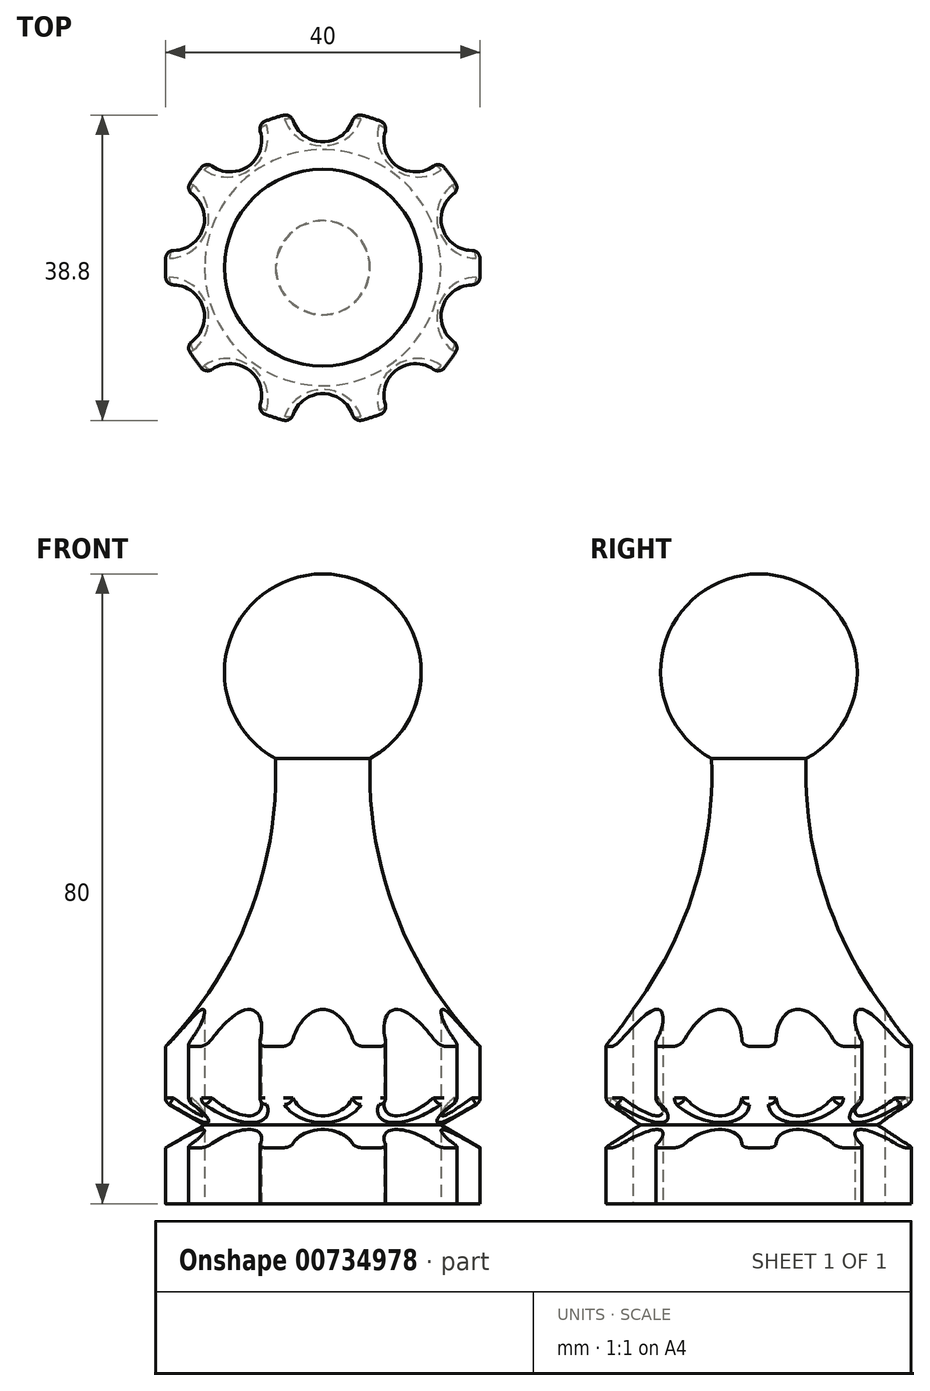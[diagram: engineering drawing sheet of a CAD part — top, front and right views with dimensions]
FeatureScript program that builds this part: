
annotation { "Feature Type Name" : "Feature", "Feature Type Description" : "" }
export const myFeature = defineFeature(function(context is Context, id is Id, definition is map)
    precondition{}
    {
        {
            var Q0;
            Q0=qCreatedBy(makeId("Front.planeOp"),FACE);
            var sketch = newSketch(context, id + "F0", { "sketchPlane" : qUnion([Q0])});
            skLineSegment(sketch, "E0", {"start": v(0, 80) * mm, "end": v(0, 0) * mm});
            skLineSegment(sketch, "E1", {"start": v(0, 0) * mm, "end": v(20, 0) * mm});
            skLineSegment(sketch, "E2", {"start": v(20, 0) * mm, "end": v(20, 7.11) * mm});
            skLineSegment(sketch, "E3", {"start": v(20, 7.11) * mm, "end": v(15, 10) * mm});
            skLineSegment(sketch, "E4", {"start": v(15, 10) * mm, "end": v(20, 12.89) * mm});
            skLineSegment(sketch, "E5", {"start": v(20, 12.89) * mm, "end": v(20, 20) * mm});
            skArc(sketch, "E6", {"start": v(6, 56.53) * mm, "mid": v(9.28, 36.84) * mm, "end": v(20, 20) * mm});
            skArc(sketch, "E7", {"start": v(6, 56.53) * mm, "mid": v(12.11, 70.6) * mm, "end": v(0, 80) * mm});
            skSolve(sketch);
        }
        {
            var Q0;
            Q0=qCreatedBy(makeId("Front.planeOp"),FACE);
            var sketch = newSketch(context, id + "F1", { "sketchPlane" : qUnion([Q0])});
            skLineSegment(sketch, "E8", {"start": v(0, -54.33) * mm, "end": v(0, 51.9) * mm, "construction": true});
            skSolve(sketch);
        }
        {
            var Q0;
            Q0 = qSketchRegion(id + "F0", true);
            var Q1;
            Q1=sQuery(id+"F1.wireOp",EDGE,"E8");
            revolve(context, id + "F2", {"surfaceOperationType" : NewSurfaceOperationType.NEW, "entities" : qUnion([Q0]), "axis" : qUnion([Q1]), "revolveType" : RevolveType.FULL});
        }
        {
            var Q0;
            Q0=makeQuery(id+"F2.opRevolve","SWEPT_FACE",FACE,{"disambiguationData":[OSD([sQuery(id+"F0.wireOp",EDGE,"E1")])]});
            var sketch = newSketch(context, id + "F3", { "sketchPlane" : qUnion([Q0])});
            skCircle(sketch, "E9", {"center": v(0, 20) * mm, "radius": 4 * mm});
            skCircle(sketch, "E10.1.0", {"center": v(-11.76, 16.18) * mm, "radius": 4 * mm});
            skCircle(sketch, "E10.2.0", {"center": v(-19.02, 6.18) * mm, "radius": 4 * mm});
            skCircle(sketch, "E10.3.0", {"center": v(-19.02, -6.18) * mm, "radius": 4 * mm});
            skCircle(sketch, "E10.4.0", {"center": v(-11.76, -16.18) * mm, "radius": 4 * mm});
            skCircle(sketch, "E10.5.0", {"center": v(0, -20) * mm, "radius": 4 * mm});
            skCircle(sketch, "E10.6.0", {"center": v(11.76, -16.18) * mm, "radius": 4 * mm});
            skCircle(sketch, "E10.7.0", {"center": v(19.02, -6.18) * mm, "radius": 4 * mm});
            skCircle(sketch, "E10.8.0", {"center": v(19.02, 6.18) * mm, "radius": 4 * mm});
            skCircle(sketch, "E10.9.0", {"center": v(11.76, 16.18) * mm, "radius": 4 * mm});
            skPoint(sketch, "E10.center", {"position": v(0, 0) * mm});
            skSolve(sketch);
        }
        {
            var Q0;
            {var subQ0=sQuery(id+"F3.wireOp",EDGE,"E9");var subQ1=makeQuery(id+"F2.opRevolve","SWEPT_EDGE",EDGE,{"disambiguationData":[OSD([sQuery(id+"F0.wireOp",EDGE,"E1"),sQuery(id+"F0.wireOp",EDGE,"E2")])]});var subQ2=makeQuery(id+"F3.imprint","INTERSECT",VERTEX,{"disambiguationData":[OD(0.0)],"derivedFrom":[subQ1,subQ0]});Q0=makeQuery(id+"F3.imprint","IMPRINT",FACE,{"disambiguationData":[TD([[makeQuery(id+"F3.imprint","IMPRINT",EDGE,{"disambiguationData":[TD([[subQ2,1.0]])],"derivedFrom":subQ0}),1.0]])]});}
            var Q1;
            {var subQ0=sQuery(id+"F3.wireOp",EDGE,"E9");var subQ1=makeQuery(id+"F2.opRevolve","SWEPT_EDGE",EDGE,{"disambiguationData":[OSD([sQuery(id+"F0.wireOp",EDGE,"E1"),sQuery(id+"F0.wireOp",EDGE,"E2")])]});var subQ2=makeQuery(id+"F3.imprint","INTERSECT",VERTEX,{"disambiguationData":[OD(0.0)],"derivedFrom":[subQ1,subQ0]});Q1=makeQuery(id+"F3.imprint","IMPRINT",FACE,{"disambiguationData":[TD([[makeQuery(id+"F3.imprint","IMPRINT",EDGE,{"disambiguationData":[TD([[subQ2,-1.0]])],"derivedFrom":subQ0}),1.0]])]});}
            var Q2;
            {var subQ0=sQuery(id+"F3.wireOp",EDGE,"E10.1.0");var subQ1=makeQuery(id+"F2.opRevolve","SWEPT_EDGE",EDGE,{"disambiguationData":[OSD([sQuery(id+"F0.wireOp",EDGE,"E1"),sQuery(id+"F0.wireOp",EDGE,"E2")])]});var subQ2=makeQuery(id+"F3.imprint","INTERSECT",VERTEX,{"disambiguationData":[OD(0.0)],"derivedFrom":[subQ1,subQ0]});Q2=makeQuery(id+"F3.imprint","IMPRINT",FACE,{"disambiguationData":[TD([[makeQuery(id+"F3.imprint","IMPRINT",EDGE,{"disambiguationData":[TD([[subQ2,-1.0]])],"derivedFrom":subQ0}),1.0]])]});}
            var Q3;
            {var subQ0=sQuery(id+"F3.wireOp",EDGE,"E10.1.0");var subQ1=makeQuery(id+"F2.opRevolve","SWEPT_EDGE",EDGE,{"disambiguationData":[OSD([sQuery(id+"F0.wireOp",EDGE,"E1"),sQuery(id+"F0.wireOp",EDGE,"E2")])]});var subQ2=makeQuery(id+"F3.imprint","INTERSECT",VERTEX,{"disambiguationData":[OD(0.0)],"derivedFrom":[subQ1,subQ0]});Q3=makeQuery(id+"F3.imprint","IMPRINT",FACE,{"disambiguationData":[TD([[makeQuery(id+"F3.imprint","IMPRINT",EDGE,{"disambiguationData":[TD([[subQ2,1.0]])],"derivedFrom":subQ0}),1.0]])]});}
            var Q4;
            {var subQ0=sQuery(id+"F3.wireOp",EDGE,"E10.2.0");var subQ1=makeQuery(id+"F2.opRevolve","SWEPT_EDGE",EDGE,{"disambiguationData":[OSD([sQuery(id+"F0.wireOp",EDGE,"E1"),sQuery(id+"F0.wireOp",EDGE,"E2")])]});var subQ2=makeQuery(id+"F3.imprint","INTERSECT",VERTEX,{"disambiguationData":[OD(0.0)],"derivedFrom":[subQ1,subQ0]});Q4=makeQuery(id+"F3.imprint","IMPRINT",FACE,{"disambiguationData":[TD([[makeQuery(id+"F3.imprint","IMPRINT",EDGE,{"disambiguationData":[TD([[subQ2,1.0]])],"derivedFrom":subQ0}),1.0]])]});}
            var Q5;
            {var subQ0=sQuery(id+"F3.wireOp",EDGE,"E10.2.0");var subQ1=makeQuery(id+"F2.opRevolve","SWEPT_EDGE",EDGE,{"disambiguationData":[OSD([sQuery(id+"F0.wireOp",EDGE,"E1"),sQuery(id+"F0.wireOp",EDGE,"E2")])]});var subQ2=makeQuery(id+"F3.imprint","INTERSECT",VERTEX,{"disambiguationData":[OD(0.0)],"derivedFrom":[subQ1,subQ0]});Q5=makeQuery(id+"F3.imprint","IMPRINT",FACE,{"disambiguationData":[TD([[makeQuery(id+"F3.imprint","IMPRINT",EDGE,{"disambiguationData":[TD([[subQ2,-1.0]])],"derivedFrom":subQ0}),1.0]])]});}
            var Q6;
            {var subQ0=sQuery(id+"F3.wireOp",EDGE,"E10.3.0");var subQ1=makeQuery(id+"F2.opRevolve","SWEPT_EDGE",EDGE,{"disambiguationData":[OSD([sQuery(id+"F0.wireOp",EDGE,"E1"),sQuery(id+"F0.wireOp",EDGE,"E2")])]});var subQ2=makeQuery(id+"F3.imprint","INTERSECT",VERTEX,{"disambiguationData":[OD(0.0)],"derivedFrom":[subQ1,subQ0]});Q6=makeQuery(id+"F3.imprint","IMPRINT",FACE,{"disambiguationData":[TD([[makeQuery(id+"F3.imprint","IMPRINT",EDGE,{"disambiguationData":[TD([[subQ2,1.0]])],"derivedFrom":subQ0}),1.0]])]});}
            var Q7;
            {var subQ0=sQuery(id+"F3.wireOp",EDGE,"E10.3.0");var subQ1=makeQuery(id+"F2.opRevolve","SWEPT_EDGE",EDGE,{"disambiguationData":[OSD([sQuery(id+"F0.wireOp",EDGE,"E1"),sQuery(id+"F0.wireOp",EDGE,"E2")])]});var subQ2=makeQuery(id+"F3.imprint","INTERSECT",VERTEX,{"disambiguationData":[OD(0.0)],"derivedFrom":[subQ1,subQ0]});Q7=makeQuery(id+"F3.imprint","IMPRINT",FACE,{"disambiguationData":[TD([[makeQuery(id+"F3.imprint","IMPRINT",EDGE,{"disambiguationData":[TD([[subQ2,-1.0]])],"derivedFrom":subQ0}),1.0]])]});}
            var Q8;
            {var subQ0=sQuery(id+"F3.wireOp",EDGE,"E10.4.0");var subQ1=makeQuery(id+"F2.opRevolve","SWEPT_EDGE",EDGE,{"disambiguationData":[OSD([sQuery(id+"F0.wireOp",EDGE,"E1"),sQuery(id+"F0.wireOp",EDGE,"E2")])]});var subQ2=makeQuery(id+"F3.imprint","INTERSECT",VERTEX,{"disambiguationData":[OD(0.0)],"derivedFrom":[subQ1,subQ0]});Q8=makeQuery(id+"F3.imprint","IMPRINT",FACE,{"disambiguationData":[TD([[makeQuery(id+"F3.imprint","IMPRINT",EDGE,{"disambiguationData":[TD([[subQ2,-1.0]])],"derivedFrom":subQ0}),1.0]])]});}
            var Q9;
            {var subQ0=sQuery(id+"F3.wireOp",EDGE,"E10.4.0");var subQ1=makeQuery(id+"F2.opRevolve","SWEPT_EDGE",EDGE,{"disambiguationData":[OSD([sQuery(id+"F0.wireOp",EDGE,"E1"),sQuery(id+"F0.wireOp",EDGE,"E2")])]});var subQ2=makeQuery(id+"F3.imprint","INTERSECT",VERTEX,{"disambiguationData":[OD(0.0)],"derivedFrom":[subQ1,subQ0]});Q9=makeQuery(id+"F3.imprint","IMPRINT",FACE,{"disambiguationData":[TD([[makeQuery(id+"F3.imprint","IMPRINT",EDGE,{"disambiguationData":[TD([[subQ2,1.0]])],"derivedFrom":subQ0}),1.0]])]});}
            var Q10;
            {var subQ0=sQuery(id+"F3.wireOp",EDGE,"E10.5.0");var subQ1=makeQuery(id+"F2.opRevolve","SWEPT_EDGE",EDGE,{"disambiguationData":[OSD([sQuery(id+"F0.wireOp",EDGE,"E1"),sQuery(id+"F0.wireOp",EDGE,"E2")])]});var subQ2=makeQuery(id+"F3.imprint","INTERSECT",VERTEX,{"disambiguationData":[OD(0.0)],"derivedFrom":[subQ1,subQ0]});Q10=makeQuery(id+"F3.imprint","IMPRINT",FACE,{"disambiguationData":[TD([[makeQuery(id+"F3.imprint","IMPRINT",EDGE,{"disambiguationData":[TD([[subQ2,-1.0]])],"derivedFrom":subQ0}),1.0]])]});}
            var Q11;
            {var subQ0=sQuery(id+"F3.wireOp",EDGE,"E10.5.0");var subQ1=makeQuery(id+"F2.opRevolve","SWEPT_EDGE",EDGE,{"disambiguationData":[OSD([sQuery(id+"F0.wireOp",EDGE,"E1"),sQuery(id+"F0.wireOp",EDGE,"E2")])]});var subQ2=makeQuery(id+"F3.imprint","INTERSECT",VERTEX,{"disambiguationData":[OD(0.0)],"derivedFrom":[subQ1,subQ0]});Q11=makeQuery(id+"F3.imprint","IMPRINT",FACE,{"disambiguationData":[TD([[makeQuery(id+"F3.imprint","IMPRINT",EDGE,{"disambiguationData":[TD([[subQ2,1.0]])],"derivedFrom":subQ0}),1.0]])]});}
            var Q12;
            {var subQ0=sQuery(id+"F3.wireOp",EDGE,"E10.6.0");var subQ1=makeQuery(id+"F2.opRevolve","SWEPT_EDGE",EDGE,{"disambiguationData":[OSD([sQuery(id+"F0.wireOp",EDGE,"E1"),sQuery(id+"F0.wireOp",EDGE,"E2")])]});var subQ2=makeQuery(id+"F3.imprint","INTERSECT",VERTEX,{"disambiguationData":[OD(0.0)],"derivedFrom":[subQ1,subQ0]});Q12=makeQuery(id+"F3.imprint","IMPRINT",FACE,{"disambiguationData":[TD([[makeQuery(id+"F3.imprint","IMPRINT",EDGE,{"disambiguationData":[TD([[subQ2,-1.0]])],"derivedFrom":subQ0}),1.0]])]});}
            var Q13;
            {var subQ0=sQuery(id+"F3.wireOp",EDGE,"E10.6.0");var subQ1=makeQuery(id+"F2.opRevolve","SWEPT_EDGE",EDGE,{"disambiguationData":[OSD([sQuery(id+"F0.wireOp",EDGE,"E1"),sQuery(id+"F0.wireOp",EDGE,"E2")])]});var subQ2=makeQuery(id+"F3.imprint","INTERSECT",VERTEX,{"disambiguationData":[OD(0.0)],"derivedFrom":[subQ1,subQ0]});Q13=makeQuery(id+"F3.imprint","IMPRINT",FACE,{"disambiguationData":[TD([[makeQuery(id+"F3.imprint","IMPRINT",EDGE,{"disambiguationData":[TD([[subQ2,1.0]])],"derivedFrom":subQ0}),1.0]])]});}
            var Q14;
            {var subQ0=sQuery(id+"F3.wireOp",EDGE,"E10.7.0");var subQ1=makeQuery(id+"F2.opRevolve","SWEPT_EDGE",EDGE,{"disambiguationData":[OSD([sQuery(id+"F0.wireOp",EDGE,"E1"),sQuery(id+"F0.wireOp",EDGE,"E2")])]});var subQ2=makeQuery(id+"F3.imprint","INTERSECT",VERTEX,{"disambiguationData":[OD(0.0)],"derivedFrom":[subQ1,subQ0]});Q14=makeQuery(id+"F3.imprint","IMPRINT",FACE,{"disambiguationData":[TD([[makeQuery(id+"F3.imprint","IMPRINT",EDGE,{"disambiguationData":[TD([[subQ2,1.0]])],"derivedFrom":subQ0}),1.0]])]});}
            var Q15;
            {var subQ0=sQuery(id+"F3.wireOp",EDGE,"E10.7.0");var subQ1=makeQuery(id+"F2.opRevolve","SWEPT_EDGE",EDGE,{"disambiguationData":[OSD([sQuery(id+"F0.wireOp",EDGE,"E1"),sQuery(id+"F0.wireOp",EDGE,"E2")])]});var subQ2=makeQuery(id+"F3.imprint","INTERSECT",VERTEX,{"disambiguationData":[OD(0.0)],"derivedFrom":[subQ1,subQ0]});Q15=makeQuery(id+"F3.imprint","IMPRINT",FACE,{"disambiguationData":[TD([[makeQuery(id+"F3.imprint","IMPRINT",EDGE,{"disambiguationData":[TD([[subQ2,-1.0]])],"derivedFrom":subQ0}),1.0]])]});}
            var Q16;
            {var subQ0=sQuery(id+"F3.wireOp",EDGE,"E10.8.0");var subQ1=makeQuery(id+"F2.opRevolve","SWEPT_EDGE",EDGE,{"disambiguationData":[OSD([sQuery(id+"F0.wireOp",EDGE,"E1"),sQuery(id+"F0.wireOp",EDGE,"E2")])]});var subQ2=makeQuery(id+"F3.imprint","INTERSECT",VERTEX,{"disambiguationData":[OD(0.0)],"derivedFrom":[subQ1,subQ0]});Q16=makeQuery(id+"F3.imprint","IMPRINT",FACE,{"disambiguationData":[TD([[makeQuery(id+"F3.imprint","IMPRINT",EDGE,{"disambiguationData":[TD([[subQ2,1.0]])],"derivedFrom":subQ0}),1.0]])]});}
            var Q17;
            {var subQ0=sQuery(id+"F3.wireOp",EDGE,"E10.8.0");var subQ1=makeQuery(id+"F2.opRevolve","SWEPT_EDGE",EDGE,{"disambiguationData":[OSD([sQuery(id+"F0.wireOp",EDGE,"E1"),sQuery(id+"F0.wireOp",EDGE,"E2")])]});var subQ2=makeQuery(id+"F3.imprint","INTERSECT",VERTEX,{"disambiguationData":[OD(0.0)],"derivedFrom":[subQ1,subQ0]});Q17=makeQuery(id+"F3.imprint","IMPRINT",FACE,{"disambiguationData":[TD([[makeQuery(id+"F3.imprint","IMPRINT",EDGE,{"disambiguationData":[TD([[subQ2,-1.0]])],"derivedFrom":subQ0}),1.0]])]});}
            var Q18;
            {var subQ0=sQuery(id+"F3.wireOp",EDGE,"E10.9.0");var subQ1=makeQuery(id+"F2.opRevolve","SWEPT_EDGE",EDGE,{"disambiguationData":[OSD([sQuery(id+"F0.wireOp",EDGE,"E1"),sQuery(id+"F0.wireOp",EDGE,"E2")])]});var subQ2=makeQuery(id+"F3.imprint","INTERSECT",VERTEX,{"disambiguationData":[OD(0.0)],"derivedFrom":[subQ1,subQ0]});Q18=makeQuery(id+"F3.imprint","IMPRINT",FACE,{"disambiguationData":[TD([[makeQuery(id+"F3.imprint","IMPRINT",EDGE,{"disambiguationData":[TD([[subQ2,-1.0]])],"derivedFrom":subQ0}),1.0]])]});}
            var Q19;
            {var subQ0=sQuery(id+"F3.wireOp",EDGE,"E10.9.0");var subQ1=makeQuery(id+"F2.opRevolve","SWEPT_EDGE",EDGE,{"disambiguationData":[OSD([sQuery(id+"F0.wireOp",EDGE,"E1"),sQuery(id+"F0.wireOp",EDGE,"E2")])]});var subQ2=makeQuery(id+"F3.imprint","INTERSECT",VERTEX,{"disambiguationData":[OD(0.0)],"derivedFrom":[subQ1,subQ0]});Q19=makeQuery(id+"F3.imprint","IMPRINT",FACE,{"disambiguationData":[TD([[makeQuery(id+"F3.imprint","IMPRINT",EDGE,{"disambiguationData":[TD([[subQ2,1.0]])],"derivedFrom":subQ0}),1.0]])]});}
            extrude(context, id + "F4", {"entities" : qUnion([Q0, Q1, Q2, Q3, Q4, Q5, Q6, Q7, Q8, Q9, Q10, Q11, Q12, Q13, Q14, Q15, Q16, Q17, Q18, Q19]), "operationType" : NewBodyOperationType.REMOVE, "oppositeDirection" : true, "depth" : 25 * mm, "offsetDistance" : 25 * mm});
        }
        {
            var Q0;
            Q0=makeQuery(id+"F4.boolean.opBoolean","INTERSECT",EDGE,{"disambiguationData":[OD(0.0)],"derivedFrom":[makeQuery(id+"F2.opRevolve","SWEPT_FACE",FACE,{"disambiguationData":[OSD([sQuery(id+"F0.wireOp",EDGE,"E5")])]}),makeQuery(id+"F4.opExtrude","SWEPT_FACE",FACE,{"disambiguationData":[OSD([sQuery(id+"F3.wireOp",EDGE,"E9")])]})]});
            var Q1;
            Q1=makeQuery(id+"F4.boolean.opBoolean","INTERSECT",EDGE,{"disambiguationData":[OD(0.0)],"derivedFrom":[makeQuery(id+"F2.opRevolve","SWEPT_FACE",FACE,{"disambiguationData":[OSD([sQuery(id+"F0.wireOp",EDGE,"E5")])]}),makeQuery(id+"F4.opExtrude","SWEPT_FACE",FACE,{"disambiguationData":[OSD([sQuery(id+"F3.wireOp",EDGE,"E10.1.0")])]})]});
            var Q2;
            Q2=makeQuery(id+"F4.boolean.opBoolean","INTERSECT",EDGE,{"disambiguationData":[OD(1.0)],"derivedFrom":[makeQuery(id+"F2.opRevolve","SWEPT_FACE",FACE,{"disambiguationData":[OSD([sQuery(id+"F0.wireOp",EDGE,"E5")])]}),makeQuery(id+"F4.opExtrude","SWEPT_FACE",FACE,{"disambiguationData":[OSD([sQuery(id+"F3.wireOp",EDGE,"E10.1.0")])]})]});
            var Q3;
            Q3=makeQuery(id+"F4.boolean.opBoolean","INTERSECT",EDGE,{"disambiguationData":[OD(0.0)],"derivedFrom":[makeQuery(id+"F2.opRevolve","SWEPT_FACE",FACE,{"disambiguationData":[OSD([sQuery(id+"F0.wireOp",EDGE,"E5")])]}),makeQuery(id+"F4.opExtrude","SWEPT_FACE",FACE,{"disambiguationData":[OSD([sQuery(id+"F3.wireOp",EDGE,"E10.2.0")])]})]});
            var Q4;
            Q4=makeQuery(id+"F4.boolean.opBoolean","INTERSECT",EDGE,{"disambiguationData":[OD(1.0)],"derivedFrom":[makeQuery(id+"F2.opRevolve","SWEPT_FACE",FACE,{"disambiguationData":[OSD([sQuery(id+"F0.wireOp",EDGE,"E5")])]}),makeQuery(id+"F4.opExtrude","SWEPT_FACE",FACE,{"disambiguationData":[OSD([sQuery(id+"F3.wireOp",EDGE,"E10.2.0")])]})]});
            var Q5;
            Q5=makeQuery(id+"F4.boolean.opBoolean","INTERSECT",EDGE,{"disambiguationData":[OD(1.0)],"derivedFrom":[makeQuery(id+"F2.opRevolve","SWEPT_FACE",FACE,{"disambiguationData":[OSD([sQuery(id+"F0.wireOp",EDGE,"E5")])]}),makeQuery(id+"F4.opExtrude","SWEPT_FACE",FACE,{"disambiguationData":[OSD([sQuery(id+"F3.wireOp",EDGE,"E9")])]})]});
            var Q6;
            Q6=makeQuery(id+"F4.boolean.opBoolean","INTERSECT",EDGE,{"disambiguationData":[OD(0.0)],"derivedFrom":[makeQuery(id+"F2.opRevolve","SWEPT_FACE",FACE,{"disambiguationData":[OSD([sQuery(id+"F0.wireOp",EDGE,"E5")])]}),makeQuery(id+"F4.opExtrude","SWEPT_FACE",FACE,{"disambiguationData":[OSD([sQuery(id+"F3.wireOp",EDGE,"E10.9.0")])]})]});
            var Q7;
            Q7=makeQuery(id+"F4.boolean.opBoolean","INTERSECT",EDGE,{"disambiguationData":[OD(1.0)],"derivedFrom":[makeQuery(id+"F2.opRevolve","SWEPT_FACE",FACE,{"disambiguationData":[OSD([sQuery(id+"F0.wireOp",EDGE,"E5")])]}),makeQuery(id+"F4.opExtrude","SWEPT_FACE",FACE,{"disambiguationData":[OSD([sQuery(id+"F3.wireOp",EDGE,"E10.9.0")])]})]});
            var Q8;
            Q8=makeQuery(id+"F4.boolean.opBoolean","INTERSECT",EDGE,{"disambiguationData":[OD(1.0)],"derivedFrom":[makeQuery(id+"F2.opRevolve","SWEPT_FACE",FACE,{"disambiguationData":[OSD([sQuery(id+"F0.wireOp",EDGE,"E5")])]}),makeQuery(id+"F4.opExtrude","SWEPT_FACE",FACE,{"disambiguationData":[OSD([sQuery(id+"F3.wireOp",EDGE,"E10.8.0")])]})]});
            var Q9;
            Q9=makeQuery(id+"F4.boolean.opBoolean","INTERSECT",EDGE,{"disambiguationData":[OD(0.0)],"derivedFrom":[makeQuery(id+"F2.opRevolve","SWEPT_FACE",FACE,{"disambiguationData":[OSD([sQuery(id+"F0.wireOp",EDGE,"E5")])]}),makeQuery(id+"F4.opExtrude","SWEPT_FACE",FACE,{"disambiguationData":[OSD([sQuery(id+"F3.wireOp",EDGE,"E10.8.0")])]})]});
            var Q10;
            Q10=makeQuery(id+"F4.boolean.opBoolean","INTERSECT",EDGE,{"disambiguationData":[OD(1.0)],"derivedFrom":[makeQuery(id+"F2.opRevolve","SWEPT_FACE",FACE,{"disambiguationData":[OSD([sQuery(id+"F0.wireOp",EDGE,"E5")])]}),makeQuery(id+"F4.opExtrude","SWEPT_FACE",FACE,{"disambiguationData":[OSD([sQuery(id+"F3.wireOp",EDGE,"E10.7.0")])]})]});
            var Q11;
            Q11=makeQuery(id+"F4.boolean.opBoolean","INTERSECT",EDGE,{"disambiguationData":[OD(0.0)],"derivedFrom":[makeQuery(id+"F2.opRevolve","SWEPT_FACE",FACE,{"disambiguationData":[OSD([sQuery(id+"F0.wireOp",EDGE,"E5")])]}),makeQuery(id+"F4.opExtrude","SWEPT_FACE",FACE,{"disambiguationData":[OSD([sQuery(id+"F3.wireOp",EDGE,"E10.7.0")])]})]});
            var Q12;
            Q12=makeQuery(id+"F4.boolean.opBoolean","INTERSECT",EDGE,{"disambiguationData":[OD(1.0)],"derivedFrom":[makeQuery(id+"F2.opRevolve","SWEPT_FACE",FACE,{"disambiguationData":[OSD([sQuery(id+"F0.wireOp",EDGE,"E5")])]}),makeQuery(id+"F4.opExtrude","SWEPT_FACE",FACE,{"disambiguationData":[OSD([sQuery(id+"F3.wireOp",EDGE,"E10.6.0")])]})]});
            var Q13;
            Q13=makeQuery(id+"F4.boolean.opBoolean","INTERSECT",EDGE,{"disambiguationData":[OD(1.0)],"derivedFrom":[makeQuery(id+"F2.opRevolve","SWEPT_FACE",FACE,{"disambiguationData":[OSD([sQuery(id+"F0.wireOp",EDGE,"E5")])]}),makeQuery(id+"F4.opExtrude","SWEPT_FACE",FACE,{"disambiguationData":[OSD([sQuery(id+"F3.wireOp",EDGE,"E10.5.0")])]})]});
            var Q14;
            Q14=makeQuery(id+"F4.boolean.opBoolean","INTERSECT",EDGE,{"disambiguationData":[OD(0.0)],"derivedFrom":[makeQuery(id+"F2.opRevolve","SWEPT_FACE",FACE,{"disambiguationData":[OSD([sQuery(id+"F0.wireOp",EDGE,"E5")])]}),makeQuery(id+"F4.opExtrude","SWEPT_FACE",FACE,{"disambiguationData":[OSD([sQuery(id+"F3.wireOp",EDGE,"E10.6.0")])]})]});
            var Q15;
            Q15=makeQuery(id+"F4.boolean.opBoolean","INTERSECT",EDGE,{"disambiguationData":[OD(0.0)],"derivedFrom":[makeQuery(id+"F2.opRevolve","SWEPT_FACE",FACE,{"disambiguationData":[OSD([sQuery(id+"F0.wireOp",EDGE,"E5")])]}),makeQuery(id+"F4.opExtrude","SWEPT_FACE",FACE,{"disambiguationData":[OSD([sQuery(id+"F3.wireOp",EDGE,"E10.5.0")])]})]});
            var Q16;
            Q16=makeQuery(id+"F4.boolean.opBoolean","INTERSECT",EDGE,{"disambiguationData":[OD(1.0)],"derivedFrom":[makeQuery(id+"F2.opRevolve","SWEPT_FACE",FACE,{"disambiguationData":[OSD([sQuery(id+"F0.wireOp",EDGE,"E5")])]}),makeQuery(id+"F4.opExtrude","SWEPT_FACE",FACE,{"disambiguationData":[OSD([sQuery(id+"F3.wireOp",EDGE,"E10.4.0")])]})]});
            var Q17;
            Q17=makeQuery(id+"F4.boolean.opBoolean","INTERSECT",EDGE,{"disambiguationData":[OD(0.0)],"derivedFrom":[makeQuery(id+"F2.opRevolve","SWEPT_FACE",FACE,{"disambiguationData":[OSD([sQuery(id+"F0.wireOp",EDGE,"E5")])]}),makeQuery(id+"F4.opExtrude","SWEPT_FACE",FACE,{"disambiguationData":[OSD([sQuery(id+"F3.wireOp",EDGE,"E10.3.0")])]})]});
            var Q18;
            Q18=makeQuery(id+"F4.boolean.opBoolean","INTERSECT",EDGE,{"disambiguationData":[OD(1.0)],"derivedFrom":[makeQuery(id+"F2.opRevolve","SWEPT_FACE",FACE,{"disambiguationData":[OSD([sQuery(id+"F0.wireOp",EDGE,"E5")])]}),makeQuery(id+"F4.opExtrude","SWEPT_FACE",FACE,{"disambiguationData":[OSD([sQuery(id+"F3.wireOp",EDGE,"E10.3.0")])]})]});
            var Q19;
            Q19=makeQuery(id+"F4.boolean.opBoolean","INTERSECT",EDGE,{"disambiguationData":[OD(0.0)],"derivedFrom":[makeQuery(id+"F2.opRevolve","SWEPT_FACE",FACE,{"disambiguationData":[OSD([sQuery(id+"F0.wireOp",EDGE,"E5")])]}),makeQuery(id+"F4.opExtrude","SWEPT_FACE",FACE,{"disambiguationData":[OSD([sQuery(id+"F3.wireOp",EDGE,"E10.4.0")])]})]});
            fillet(context, id + "F5", {"entities" : qUnion([Q0, Q1, Q2, Q3, Q4, Q5, Q6, Q7, Q8, Q9, Q10, Q11, Q12, Q13, Q14, Q15, Q16, Q17, Q18, Q19]), "radius" : 1 * mm, "tangentPropagation" : true, "allowEdgeOverflow" : false});
        }
        {
            var Q0;
            Q0=makeQuery(id+"F4.boolean.opBoolean","INTERSECT",EDGE,{"disambiguationData":[OD(1.0)],"derivedFrom":[makeQuery(id+"F2.opRevolve","SWEPT_FACE",FACE,{"disambiguationData":[OSD([sQuery(id+"F0.wireOp",EDGE,"E2")])]}),makeQuery(id+"F4.opExtrude","SWEPT_FACE",FACE,{"disambiguationData":[OSD([sQuery(id+"F3.wireOp",EDGE,"E10.6.0")])]})]});
            var Q1;
            Q1=makeQuery(id+"F4.boolean.opBoolean","INTERSECT",EDGE,{"disambiguationData":[OD(0.0)],"derivedFrom":[makeQuery(id+"F2.opRevolve","SWEPT_FACE",FACE,{"disambiguationData":[OSD([sQuery(id+"F0.wireOp",EDGE,"E2")])]}),makeQuery(id+"F4.opExtrude","SWEPT_FACE",FACE,{"disambiguationData":[OSD([sQuery(id+"F3.wireOp",EDGE,"E10.7.0")])]})]});
            var Q2;
            Q2=makeQuery(id+"F4.boolean.opBoolean","INTERSECT",EDGE,{"disambiguationData":[OD(0.0)],"derivedFrom":[makeQuery(id+"F2.opRevolve","SWEPT_FACE",FACE,{"disambiguationData":[OSD([sQuery(id+"F0.wireOp",EDGE,"E2")])]}),makeQuery(id+"F4.opExtrude","SWEPT_FACE",FACE,{"disambiguationData":[OSD([sQuery(id+"F3.wireOp",EDGE,"E10.6.0")])]})]});
            var Q3;
            Q3=makeQuery(id+"F4.boolean.opBoolean","INTERSECT",EDGE,{"disambiguationData":[OD(1.0)],"derivedFrom":[makeQuery(id+"F2.opRevolve","SWEPT_FACE",FACE,{"disambiguationData":[OSD([sQuery(id+"F0.wireOp",EDGE,"E2")])]}),makeQuery(id+"F4.opExtrude","SWEPT_FACE",FACE,{"disambiguationData":[OSD([sQuery(id+"F3.wireOp",EDGE,"E10.5.0")])]})]});
            var Q4;
            Q4=makeQuery(id+"F4.boolean.opBoolean","INTERSECT",EDGE,{"disambiguationData":[OD(0.0)],"derivedFrom":[makeQuery(id+"F2.opRevolve","SWEPT_FACE",FACE,{"disambiguationData":[OSD([sQuery(id+"F0.wireOp",EDGE,"E2")])]}),makeQuery(id+"F4.opExtrude","SWEPT_FACE",FACE,{"disambiguationData":[OSD([sQuery(id+"F3.wireOp",EDGE,"E10.5.0")])]})]});
            var Q5;
            Q5=makeQuery(id+"F4.boolean.opBoolean","INTERSECT",EDGE,{"disambiguationData":[OD(1.0)],"derivedFrom":[makeQuery(id+"F2.opRevolve","SWEPT_FACE",FACE,{"disambiguationData":[OSD([sQuery(id+"F0.wireOp",EDGE,"E2")])]}),makeQuery(id+"F4.opExtrude","SWEPT_FACE",FACE,{"disambiguationData":[OSD([sQuery(id+"F3.wireOp",EDGE,"E10.4.0")])]})]});
            var Q6;
            Q6=makeQuery(id+"F4.boolean.opBoolean","INTERSECT",EDGE,{"disambiguationData":[OD(1.0)],"derivedFrom":[makeQuery(id+"F2.opRevolve","SWEPT_FACE",FACE,{"disambiguationData":[OSD([sQuery(id+"F0.wireOp",EDGE,"E2")])]}),makeQuery(id+"F4.opExtrude","SWEPT_FACE",FACE,{"disambiguationData":[OSD([sQuery(id+"F3.wireOp",EDGE,"E10.7.0")])]})]});
            var Q7;
            Q7=makeQuery(id+"F4.boolean.opBoolean","INTERSECT",EDGE,{"disambiguationData":[OD(0.0)],"derivedFrom":[makeQuery(id+"F2.opRevolve","SWEPT_FACE",FACE,{"disambiguationData":[OSD([sQuery(id+"F0.wireOp",EDGE,"E2")])]}),makeQuery(id+"F4.opExtrude","SWEPT_FACE",FACE,{"disambiguationData":[OSD([sQuery(id+"F3.wireOp",EDGE,"E10.8.0")])]})]});
            var Q8;
            Q8=makeQuery(id+"F4.boolean.opBoolean","INTERSECT",EDGE,{"disambiguationData":[OD(0.0)],"derivedFrom":[makeQuery(id+"F2.opRevolve","SWEPT_FACE",FACE,{"disambiguationData":[OSD([sQuery(id+"F0.wireOp",EDGE,"E2")])]}),makeQuery(id+"F4.opExtrude","SWEPT_FACE",FACE,{"disambiguationData":[OSD([sQuery(id+"F3.wireOp",EDGE,"E10.4.0")])]})]});
            var Q9;
            Q9=makeQuery(id+"F4.boolean.opBoolean","INTERSECT",EDGE,{"disambiguationData":[OD(1.0)],"derivedFrom":[makeQuery(id+"F2.opRevolve","SWEPT_FACE",FACE,{"disambiguationData":[OSD([sQuery(id+"F0.wireOp",EDGE,"E2")])]}),makeQuery(id+"F4.opExtrude","SWEPT_FACE",FACE,{"disambiguationData":[OSD([sQuery(id+"F3.wireOp",EDGE,"E10.3.0")])]})]});
            var Q10;
            Q10=makeQuery(id+"F4.boolean.opBoolean","INTERSECT",EDGE,{"disambiguationData":[OD(1.0)],"derivedFrom":[makeQuery(id+"F2.opRevolve","SWEPT_FACE",FACE,{"disambiguationData":[OSD([sQuery(id+"F0.wireOp",EDGE,"E2")])]}),makeQuery(id+"F4.opExtrude","SWEPT_FACE",FACE,{"disambiguationData":[OSD([sQuery(id+"F3.wireOp",EDGE,"E10.1.0")])]})]});
            var Q11;
            Q11=makeQuery(id+"F4.boolean.opBoolean","INTERSECT",EDGE,{"disambiguationData":[OD(0.0)],"derivedFrom":[makeQuery(id+"F2.opRevolve","SWEPT_FACE",FACE,{"disambiguationData":[OSD([sQuery(id+"F0.wireOp",EDGE,"E2")])]}),makeQuery(id+"F4.opExtrude","SWEPT_FACE",FACE,{"disambiguationData":[OSD([sQuery(id+"F3.wireOp",EDGE,"E10.1.0")])]})]});
            var Q12;
            Q12=makeQuery(id+"F4.boolean.opBoolean","INTERSECT",EDGE,{"disambiguationData":[OD(0.0)],"derivedFrom":[makeQuery(id+"F2.opRevolve","SWEPT_FACE",FACE,{"disambiguationData":[OSD([sQuery(id+"F0.wireOp",EDGE,"E2")])]}),makeQuery(id+"F4.opExtrude","SWEPT_FACE",FACE,{"disambiguationData":[OSD([sQuery(id+"F3.wireOp",EDGE,"E9")])]})]});
            var Q13;
            Q13=makeQuery(id+"F4.boolean.opBoolean","INTERSECT",EDGE,{"disambiguationData":[OD(1.0)],"derivedFrom":[makeQuery(id+"F2.opRevolve","SWEPT_FACE",FACE,{"disambiguationData":[OSD([sQuery(id+"F0.wireOp",EDGE,"E2")])]}),makeQuery(id+"F4.opExtrude","SWEPT_FACE",FACE,{"disambiguationData":[OSD([sQuery(id+"F3.wireOp",EDGE,"E9")])]})]});
            var Q14;
            Q14=makeQuery(id+"F4.boolean.opBoolean","INTERSECT",EDGE,{"disambiguationData":[OD(0.0)],"derivedFrom":[makeQuery(id+"F2.opRevolve","SWEPT_FACE",FACE,{"disambiguationData":[OSD([sQuery(id+"F0.wireOp",EDGE,"E2")])]}),makeQuery(id+"F4.opExtrude","SWEPT_FACE",FACE,{"disambiguationData":[OSD([sQuery(id+"F3.wireOp",EDGE,"E10.9.0")])]})]});
            var Q15;
            Q15=makeQuery(id+"F4.boolean.opBoolean","INTERSECT",EDGE,{"disambiguationData":[OD(1.0)],"derivedFrom":[makeQuery(id+"F2.opRevolve","SWEPT_FACE",FACE,{"disambiguationData":[OSD([sQuery(id+"F0.wireOp",EDGE,"E2")])]}),makeQuery(id+"F4.opExtrude","SWEPT_FACE",FACE,{"disambiguationData":[OSD([sQuery(id+"F3.wireOp",EDGE,"E10.9.0")])]})]});
            var Q16;
            Q16=makeQuery(id+"F4.boolean.opBoolean","INTERSECT",EDGE,{"disambiguationData":[OD(1.0)],"derivedFrom":[makeQuery(id+"F2.opRevolve","SWEPT_FACE",FACE,{"disambiguationData":[OSD([sQuery(id+"F0.wireOp",EDGE,"E2")])]}),makeQuery(id+"F4.opExtrude","SWEPT_FACE",FACE,{"disambiguationData":[OSD([sQuery(id+"F3.wireOp",EDGE,"E10.8.0")])]})]});
            var Q17;
            Q17=makeQuery(id+"F4.boolean.opBoolean","INTERSECT",EDGE,{"disambiguationData":[OD(0.0)],"derivedFrom":[makeQuery(id+"F2.opRevolve","SWEPT_FACE",FACE,{"disambiguationData":[OSD([sQuery(id+"F0.wireOp",EDGE,"E2")])]}),makeQuery(id+"F4.opExtrude","SWEPT_FACE",FACE,{"disambiguationData":[OSD([sQuery(id+"F3.wireOp",EDGE,"E10.3.0")])]})]});
            var Q18;
            Q18=makeQuery(id+"F4.boolean.opBoolean","INTERSECT",EDGE,{"disambiguationData":[OD(1.0)],"derivedFrom":[makeQuery(id+"F2.opRevolve","SWEPT_FACE",FACE,{"disambiguationData":[OSD([sQuery(id+"F0.wireOp",EDGE,"E2")])]}),makeQuery(id+"F4.opExtrude","SWEPT_FACE",FACE,{"disambiguationData":[OSD([sQuery(id+"F3.wireOp",EDGE,"E10.2.0")])]})]});
            var Q19;
            Q19=makeQuery(id+"F4.boolean.opBoolean","INTERSECT",EDGE,{"disambiguationData":[OD(0.0)],"derivedFrom":[makeQuery(id+"F2.opRevolve","SWEPT_FACE",FACE,{"disambiguationData":[OSD([sQuery(id+"F0.wireOp",EDGE,"E2")])]}),makeQuery(id+"F4.opExtrude","SWEPT_FACE",FACE,{"disambiguationData":[OSD([sQuery(id+"F3.wireOp",EDGE,"E10.2.0")])]})]});
            var Q20;
            Q20=makeQuery(id+"F4.boolean.opBoolean","INTERSECT",EDGE,{"derivedFrom":[makeQuery(id+"F2.opRevolve","SWEPT_FACE",FACE,{"disambiguationData":[OSD([sQuery(id+"F0.wireOp",EDGE,"E4")])]}),makeQuery(id+"F4.opExtrude","SWEPT_FACE",FACE,{"disambiguationData":[OSD([sQuery(id+"F3.wireOp",EDGE,"E10.8.0")])]})]});
            var Q21;
            Q21=makeQuery(id+"F4.boolean.opBoolean","INTERSECT",EDGE,{"derivedFrom":[makeQuery(id+"F2.opRevolve","SWEPT_FACE",FACE,{"disambiguationData":[OSD([sQuery(id+"F0.wireOp",EDGE,"E4")])]}),makeQuery(id+"F4.opExtrude","SWEPT_FACE",FACE,{"disambiguationData":[OSD([sQuery(id+"F3.wireOp",EDGE,"E10.9.0")])]})]});
            fillet(context, id + "F6", {"entities" : qUnion([Q0, Q1, Q2, Q3, Q4, Q5, Q6, Q7, Q8, Q9, Q10, Q11, Q12, Q13, Q14, Q15, Q16, Q17, Q18, Q19, Q20, Q21]), "radius" : 1 * mm, "tangentPropagation" : true, "allowEdgeOverflow" : false});
        }
    });
